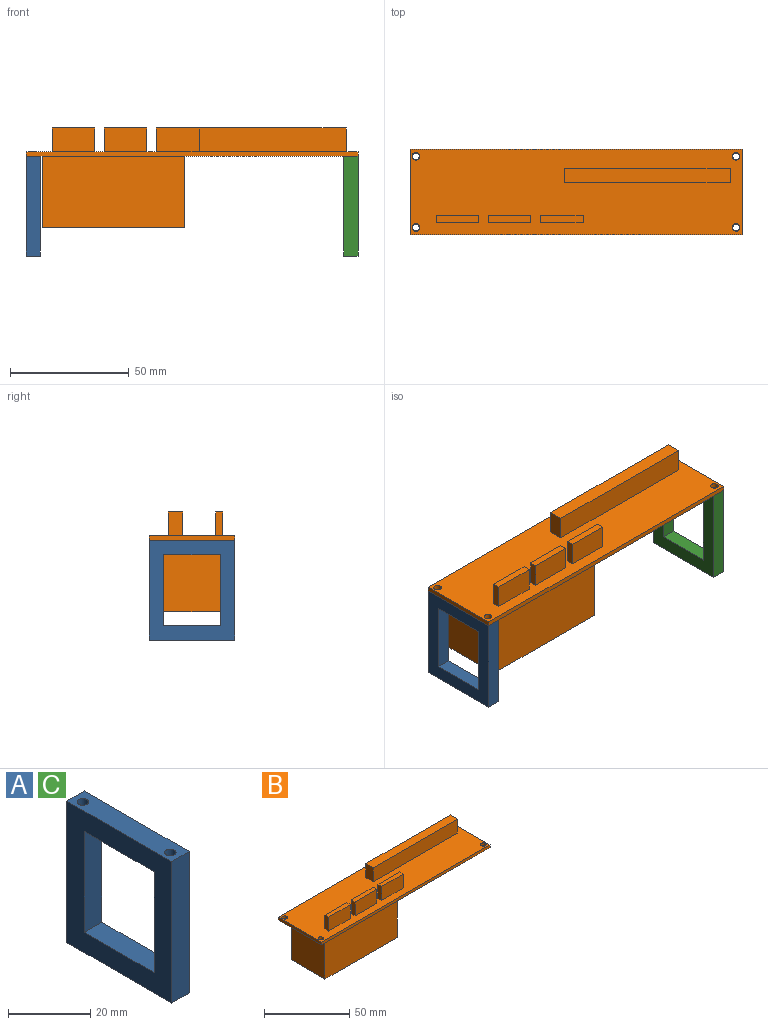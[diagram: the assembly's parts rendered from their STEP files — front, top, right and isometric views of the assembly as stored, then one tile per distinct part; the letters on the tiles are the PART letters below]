
ASSEMBLY  parts=3 mates=2
PART A: 12 faces, bbox 6x36x42 mm
  f0: plane 24x6mm, normal (0,0,1), area 144mm2, adj f1,f3,f6,f7
  f1: plane 42x36mm, normal (1,0,0), area 792mm2, adj f0,f2,f4,f5,f6,f7,f8,f9
  f2: plane 42x6mm, normal (0,1,0), area 252mm2, adj f1,f3,f5,f9
  f3: plane 42x36mm, normal (-1,0,0), area 792mm2, adj f0,f2,f4,f5,f6,f7,f8,f9
  f4: plane 42x6mm, normal (0,-1,0), area 252mm2, adj f1,f3,f5,f9
  f5: plane 36x6mm, normal (0,0,-1), area 203.7mm2, adj f1,f2,f3,f4,f10,f11
  f6: plane 30x6mm, normal (0,-1,0), area 180mm2, adj f0,f1,f3,f8
  f7: plane 30x6mm, normal (0,1,0), area 180mm2, adj f0,f1,f3,f8
  f8: plane 24x6mm, normal (0,0,-1), area 144mm2, adj f1,f3,f6,f7
  f9: plane 36x6mm, normal (0,0,1), area 203.7mm2, adj f1,f2,f3,f4,f10,f11
  f10: cylinder r=1.4mm len=42mm, axis (0,0,1), area 369.5mm2, adj f5,f9
  f11: cylinder r=1.4mm len=42mm, axis (0,0,1), area 369.5mm2, adj f5,f9
PART B: 35 faces, bbox 140x36x42 mm
  f0: plane 140x36mm, normal (0,0,1), area 4425.8mm2, adj f1,f2,f3,f4,f5,f6,f7,f8
  f1: plane 36x2mm, normal (1,0,0), area 72mm2, adj f0,f2,f7,f9
  f2: plane 140x2mm, normal (0,1,0), area 280mm2, adj f0,f1,f3,f9
  f3: plane 36x2mm, normal (-1,0,0), area 72mm2, adj f0,f2,f7,f9
  f4: cylinder r=1.6mm len=3.2mm, axis (0,0,-1), area 20.1mm2, adj f0,f9
  f5: cylinder r=1.6mm len=3.2mm, axis (0,0,-1), area 20.1mm2, adj f0,f9
  f6: cylinder r=1.6mm len=3.2mm, axis (0,0,-1), area 20.1mm2, adj f0,f9
  f7: plane 140x2mm, normal (0,-1,0), area 280mm2, adj f0,f1,f3,f9
  f8: cylinder r=1.6mm len=3.2mm, axis (0,0,-1), area 20.1mm2, adj f0,f9
  f9: plane 140x36mm, normal (0,0,-1), area 3327.8mm2, adj f1,f2,f3,f4,f5,f6,f7,f8
  f10: plane 30x28mm, normal (1,0,0), area 840mm2, adj f9,f11,f13,f14
  f11: plane 60x30mm, normal (0,-1,0), area 1800mm2, adj f9,f10,f12,f14
  f12: plane 30x28mm, normal (-1,0,0), area 840mm2, adj f9,f11,f13,f14
  f13: plane 60x30mm, normal (0,1,0), area 1800mm2, adj f9,f10,f12,f14
  f14: plane 60x28mm, normal (0,0,-1), area 1680mm2, adj f10,f11,f12,f13
  f15: plane 70x10mm, normal (0,-1,0), area 700mm2, adj f0,f16,f18,f19
  f16: plane 10x6mm, normal (1,0,0), area 60mm2, adj f0,f15,f17,f19
  f17: plane 70x10mm, normal (0,1,0), area 700mm2, adj f0,f16,f18,f19
  f18: plane 10x6mm, normal (-1,0,0), area 60mm2, adj f0,f15,f17,f19
  f19: plane 70x6mm, normal (0,0,1), area 420mm2, adj f15,f16,f17,f18
  f20: plane 18x10mm, normal (0,1,0), area 180mm2, adj f0,f21,f23,f24
  f21: plane 10x3mm, normal (-1,0,0), area 30mm2, adj f0,f20,f22,f24
  f22: plane 18x10mm, normal (0,-1,0), area 180mm2, adj f0,f21,f23,f24
  f23: plane 10x3mm, normal (1,0,0), area 30mm2, adj f0,f20,f22,f24
  f24: plane 18x3mm, normal (0,0,1), area 54mm2, adj f20,f21,f22,f23
  f25: plane 18x10mm, normal (0,1,0), area 180mm2, adj f0,f26,f28,f29
  f26: plane 10x3mm, normal (-1,0,0), area 30mm2, adj f0,f25,f27,f29
  f27: plane 18x10mm, normal (0,-1,0), area 180mm2, adj f0,f26,f28,f29
  f28: plane 10x3mm, normal (1,0,0), area 30mm2, adj f0,f25,f27,f29
  f29: plane 18x3mm, normal (0,0,1), area 54mm2, adj f25,f26,f27,f28
  f30: plane 18x10mm, normal (0,1,0), area 180mm2, adj f0,f31,f33,f34
  f31: plane 10x3mm, normal (-1,0,0), area 30mm2, adj f0,f30,f32,f34
  f32: plane 18x10mm, normal (0,-1,0), area 180mm2, adj f0,f31,f33,f34
  f33: plane 10x3mm, normal (1,0,0), area 30mm2, adj f0,f30,f32,f34
  f34: plane 18x3mm, normal (0,0,1), area 54mm2, adj f30,f31,f32,f33
PART C: same geometry as A
PLACE A rot(axis=(1,0,0),180deg) t=(-61,-12.97,12.88)mm
PLACE B t=(6.5,2.03,12.88)mm
PLACE C rot(axis=(0,1,0),180deg) t=(74,17.03,12.88)mm
MATE fastened C.f10 <-> B.f5  axis (0,0,1) through (74,17.03,12.88)mm
MATE fastened A.f10 <-> B.f8  axis (0,0,1) through (-61,-12.97,12.88)mm
